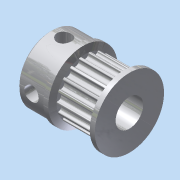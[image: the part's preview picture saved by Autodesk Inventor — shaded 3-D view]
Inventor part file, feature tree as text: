
AUTODESK INVENTOR PART (.ipt)
format: ipt  version: 2015 (Build 190159000, 159)  size: 393,216 bytes
history: native  units: in
note: dims shown in document units (in); Inventor stores cm internally (conversion verified against a paired STEP export)
features: other x1, extrude x1, imported_body x1, sketch x1
ambient origin geometry x8: Origin, YZ Plane, XZ Plane, XY Plane, X Axis, Y Axis, Z Axis, Center Point
bodies: Solid1 (feature_tree)
feature tree (4):
  other  "43184-G1"
  extrude  "Extrusion1"  Depth=1.0in TaperAngle=0.0deg
  imported_body  "Base1"
  sketch  "Sketch1"  dims[d0=0.315in d1=1.0in d2=0.0in]
